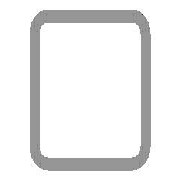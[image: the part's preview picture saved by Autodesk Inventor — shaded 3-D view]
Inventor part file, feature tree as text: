
AUTODESK INVENTOR PART (.ipt)
format: ipt  version: 2025.1 (Build 291241020, 241B)  size: 135,168 bytes
history: native  units: mm (DEFAULTED — no unit token found)
features: other x4, sketch x1, plane x1
ambient origin geometry x8: Origin, YZ Plane, XZ Plane, XY Plane, X Axis, Y Axis, Z Axis, Center Point
bodies: Solid1 (feature_tree), Body (feature_tree)
feature tree (6):
  parser-record x1  (decoder bookkeeping rows leaked as tree rows — omitted from the tree; the rows remain in map.json)
  other  "Driven Length"
  other  "Start Plane"
  other  "End Plane"
  sketch  "Sketch3"  dims[d3=120.0mm d4=0.0mm d7=4.0mm d9=40.0mm d11=40.0mm d12=2.0mm d13=40.0mm d14=160.0mm d15=20.0mm d16=20.0mm d17=90.0deg d18=120.0mm]
  plane  "Work Plane3"
